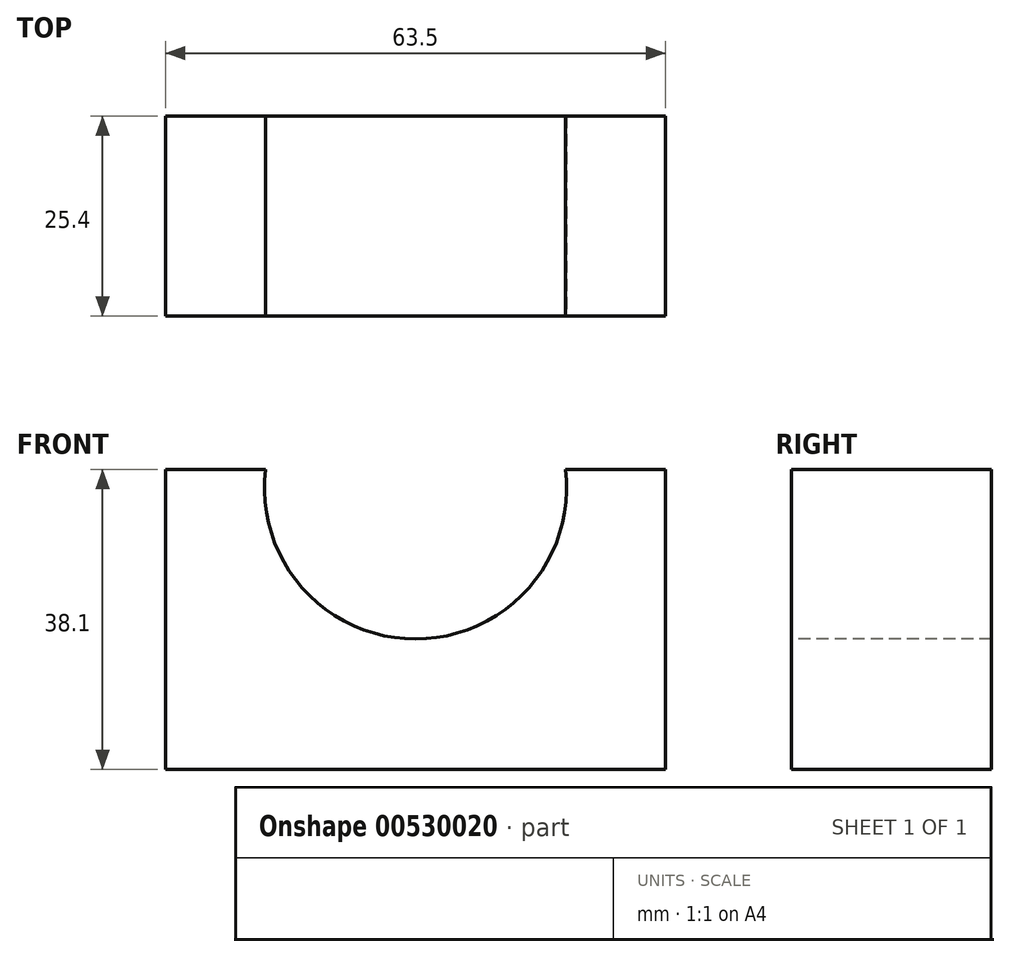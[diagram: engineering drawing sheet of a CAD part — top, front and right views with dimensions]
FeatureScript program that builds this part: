
annotation { "Feature Type Name" : "Feature", "Feature Type Description" : "" }
export const myFeature = defineFeature(function(context is Context, id is Id, definition is map)
    precondition{}
    {
        {
            var Q0;
            Q0=qCreatedBy(makeId("Front.planeOp"),FACE);
            var sketch = newSketch(context, id + "F0", { "sketchPlane" : qUnion([Q0])});
            skLineSegment(sketch, "E0", {"start": v(-69.68, 40.58) * mm, "end": v(-69.68, 2.48) * mm});
            skLineSegment(sketch, "E1", {"start": v(-69.68, 40.58) * mm, "end": v(-6.18, 40.58) * mm});
            skLineSegment(sketch, "E2", {"start": v(-6.18, 40.58) * mm, "end": v(-6.18, 2.48) * mm});
            skLineSegment(sketch, "E3", {"start": v(-69.68, 2.48) * mm, "end": v(-6.18, 2.48) * mm});
            skSolve(sketch);
        }
        {
            var Q0;
            Q0=makeQuery(id+"F0.imprint","IMPRINT",FACE,{"disambiguationData":[TD([[makeQuery(id+"F0.imprint","IMPRINT",EDGE,{"derivedFrom":sQuery(id+"F0.wireOp",EDGE,"E0")}),1.0]])]});
            extrude(context, id + "F1", {"entities" : qUnion([Q0]), "depth" : 25.4 * mm, "offsetDistance" : 25.4 * mm});
        }
        {
            var Q0;
            Q0=makeQuery(id+"F1.opExtrude","CAP_FACE",FACE,{"disambiguationData":[OSD([sQuery(id+"F0.wireOp",EDGE,"E0"),sQuery(id+"F0.wireOp",EDGE,"E1"),sQuery(id+"F0.wireOp",EDGE,"E2"),sQuery(id+"F0.wireOp",EDGE,"E3")])],"isStart":false});
            var sketch = newSketch(context, id + "F2", { "sketchPlane" : qUnion([Q0])});
            skArc(sketch, "E4", {"start": v(-56.98, 40.58) * mm, "mid": v(-37.93, 19.05) * mm, "end": v(-18.88, 40.58) * mm});
            skLineSegment(sketch, "E5", {"start": v(-56.98, 40.58) * mm, "end": v(-69.68, 40.58) * mm});
            skLineSegment(sketch, "E6", {"start": v(-18.88, 40.58) * mm, "end": v(-6.18, 40.58) * mm});
            skLineSegment(sketch, "E7", {"start": v(-56.98, 40.58) * mm, "end": v(-18.88, 40.58) * mm});
            skSolve(sketch);
        }
        {
            var Q0;
            Q0=makeQuery(id+"F2.imprint","IMPRINT",FACE,{"disambiguationData":[TD([[makeQuery(id+"F2.imprint","IMPRINT",EDGE,{"derivedFrom":sQuery(id+"F2.wireOp",EDGE,"E4")}),1.0]])]});
            extrude(context, id + "F3", {"entities" : qUnion([Q0]), "operationType" : NewBodyOperationType.REMOVE, "endBound" : BoundingType.THROUGH_ALL, "oppositeDirection" : true, "depth" : 25.4 * mm, "offsetDistance" : 25.4 * mm});
        }
    });
